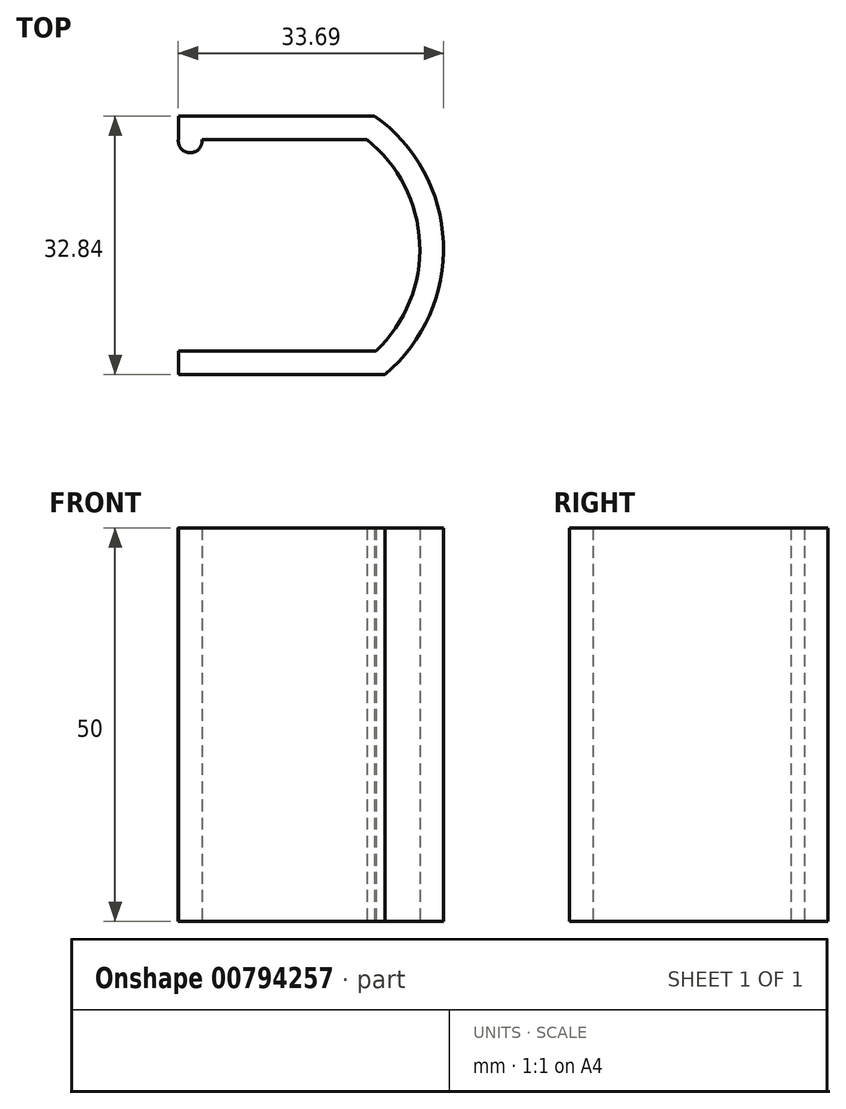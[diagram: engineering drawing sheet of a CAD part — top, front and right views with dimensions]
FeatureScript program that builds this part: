
annotation { "Feature Type Name" : "Feature", "Feature Type Description" : "" }
export const myFeature = defineFeature(function(context is Context, id is Id, definition is map)
    precondition{}
    {
        {
            var Q0;
            Q0=qCreatedBy(makeId("Top.planeOp"),FACE);
            var sketch = newSketch(context, id + "F0", { "sketchPlane" : qUnion([Q0])});
            skLineSegment(sketch, "E0", {"start": v(0, 0) * mm, "end": v(15.68, 0) * mm, "construction": true});
            skPoint(sketch, "E1", {"position": v(0, -13.42) * mm});
            skPoint(sketch, "E2", {"position": v(0, 13.42) * mm});
            skLineSegment(sketch, "E3", {"start": v(0, 13.42) * mm, "end": v(0, -13.42) * mm, "construction": true});
            skLineSegment(sketch, "E4", {"start": v(8.94, 13.42) * mm, "end": v(0, 13.42) * mm});
            skLineSegment(sketch, "E5", {"start": v(10.12, -13.42) * mm, "end": v(0, -13.42) * mm});
            skArc(sketch, "E6", {"start": v(10.13, -13.42) * mm, "mid": v(15.67, 0.27) * mm, "end": v(8.94, 13.42) * mm});
            skLineSegment(sketch, "E7.0", {"start": v(9.94, 16.42) * mm, "end": v(0, 16.42) * mm});
            skArc(sketch, "E7.1", {"start": v(11.27, -16.42) * mm, "mid": v(18.67, 0.33) * mm, "end": v(9.94, 16.42) * mm});
            skLineSegment(sketch, "E7.2", {"start": v(11.27, -16.42) * mm, "end": v(0, -16.42) * mm});
            skLineSegment(sketch, "E8", {"start": v(0, 16.42) * mm, "end": v(0, 13.42) * mm});
            skLineSegment(sketch, "E9", {"start": v(0, -13.42) * mm, "end": v(0, -16.42) * mm});
            skSolve(sketch);
        }
        {
            var Q0;
            Q0 = qSketchRegion(id + "F0", true);
            extrude(context, id + "F1", {"entities" : qUnion([Q0]), "depth" : 50 * mm, "offsetDistance" : 25 * mm});
        }
        {
            var Q0;
            Q0=makeQuery(id+"F1.opExtrude","SWEPT_FACE",FACE,{"disambiguationData":[OSD([sQuery(id+"F0.wireOp",EDGE,"E8")])]});
            var sketch = newSketch(context, id + "F2", { "sketchPlane" : qUnion([Q0])});
            skLineSegment(sketch, "E10.bottom", {"start": v(-16.42, 50) * mm, "end": v(-13.42, 50) * mm});
            skLineSegment(sketch, "E10.top", {"start": v(-16.42, 0) * mm, "end": v(-13.42, 0) * mm});
            skLineSegment(sketch, "E10.left", {"start": v(-16.42, 50) * mm, "end": v(-16.42, 0) * mm});
            skLineSegment(sketch, "E10.right", {"start": v(-13.42, 50) * mm, "end": v(-13.42, 0) * mm});
            skSolve(sketch);
        }
        {
            var Q0;
            Q0=makeQuery(id+"F2.imprint","IMPRINT",FACE,{"disambiguationData":[TD([[makeQuery(id+"F2.imprint","IMPRINT",EDGE,{"derivedFrom":sQuery(id+"F2.wireOp",EDGE,"E10.bottom")}),-1.0]])]});
            extrude(context, id + "F3", {"entities" : qUnion([Q0]), "operationType" : NewBodyOperationType.ADD, "depth" : 15 * mm, "offsetDistance" : 25 * mm});
        }
        {
            var Q0;
            Q0=makeQuery(id+"F1.opExtrude","SWEPT_FACE",FACE,{"disambiguationData":[OSD([sQuery(id+"F0.wireOp",EDGE,"E9")])]});
            var sketch = newSketch(context, id + "F4", { "sketchPlane" : qUnion([Q0])});
            skLineSegment(sketch, "E11.bottom", {"start": v(13.42, 50) * mm, "end": v(16.42, 50) * mm});
            skLineSegment(sketch, "E11.top", {"start": v(13.42, 0) * mm, "end": v(16.42, 0) * mm});
            skLineSegment(sketch, "E11.left", {"start": v(13.42, 50) * mm, "end": v(13.42, 0) * mm});
            skLineSegment(sketch, "E11.right", {"start": v(16.42, 50) * mm, "end": v(16.42, 0) * mm});
            skSolve(sketch);
        }
        {
            var Q0;
            Q0=makeQuery(id+"F4.imprint","IMPRINT",FACE,{"disambiguationData":[TD([[makeQuery(id+"F4.imprint","IMPRINT",EDGE,{"derivedFrom":sQuery(id+"F4.wireOp",EDGE,"E11.bottom")}),-1.0]])]});
            extrude(context, id + "F5", {"entities" : qUnion([Q0]), "operationType" : NewBodyOperationType.ADD, "depth" : 15 * mm, "offsetDistance" : 25 * mm});
        }
        {
            var Q0;
            Q0=makeQuery(id+"F1.opExtrude","SWEPT_EDGE",EDGE,{"disambiguationData":[OSD([sQuery(id+"F0.wireOp",EDGE,"E7.0"),sQuery(id+"F0.wireOp",EDGE,"E7.1")])]});
            cPlane(context, id + "F6", {"entities" : qUnion([Q0]), "cplaneType" : CPlaneType.LINE_ANGLE, "offset" : 25 * mm, "angle" : 67.06 * degree, "oppositeDirection" : true, "width" : 150 * mm, "height" : 150 * mm});
        }
        {
            var Q0;
            Q0=qCreatedBy(id+"F6.planeOp",FACE);
            var sketch = newSketch(context, id + "F7", { "sketchPlane" : qUnion([Q0])});
            skPoint(sketch, "E12", {"position": v(2.75, 13.58) * mm});
            skLineSegment(sketch, "E13.bottom", {"start": v(6.46, 11.07) * mm, "end": v(1.53, 9.28) * mm});
            skLineSegment(sketch, "E13.top", {"start": v(3.98, 17.89) * mm, "end": v(-0.95, 16.1) * mm});
            skLineSegment(sketch, "E13.left", {"start": v(7.65, 13.64) * mm, "end": v(6.54, 16.7) * mm});
            skLineSegment(sketch, "E13.right", {"start": v(-1.04, 10.47) * mm, "end": v(-2.15, 13.53) * mm});
            skPoint(sketch, "E14.visualSharp", {"position": v(-2.83, 15.4) * mm});
            skArc(sketch, "E14.filletArc", {"start": v(-0.95, 16.1) * mm, "mid": v(-2.08, 15.06) * mm, "end": v(-2.15, 13.53) * mm});
            skPoint(sketch, "E15.visualSharp", {"position": v(5.86, 18.57) * mm});
            skArc(sketch, "E15.filletArc", {"start": v(6.54, 16.7) * mm, "mid": v(5.5, 17.82) * mm, "end": v(3.98, 17.89) * mm});
            skPoint(sketch, "E16.visualSharp", {"position": v(8.34, 11.76) * mm});
            skArc(sketch, "E16.filletArc", {"start": v(6.46, 11.07) * mm, "mid": v(7.59, 12.1) * mm, "end": v(7.65, 13.64) * mm});
            skPoint(sketch, "E17.visualSharp", {"position": v(-0.35, 8.6) * mm});
            skArc(sketch, "E17.filletArc", {"start": v(-1.04, 10.47) * mm, "mid": v(0, 9.34) * mm, "end": v(1.53, 9.28) * mm});
            skLineSegment(sketch, "E18", {"start": v(-2.58, 14.34) * mm, "end": v(7.1, 15.16) * mm, "construction": true});
            skPoint(sketch, "E18.startSnap0", {"position": v(-1.6, 12) * mm});
            skSolve(sketch);
        }
        {
            var Q0;
            Q0=qCreatedBy(makeId("Top.planeOp"),FACE);
            var sketch = newSketch(context, id + "F8", { "sketchPlane" : qUnion([Q0])});
            skLineSegment(sketch, "E19", {"start": v(-15, 13.42) * mm, "end": v(-12, 13.42) * mm});
            skArc(sketch, "E20", {"start": v(-15, 13.42) * mm, "mid": v(-13.5, 11.74) * mm, "end": v(-12, 13.42) * mm});
            skSolve(sketch);
        }
        {
            var Q0;
            Q0=makeQuery(id+"F8.imprint","IMPRINT",FACE,{"disambiguationData":[TD([[makeQuery(id+"F8.imprint","IMPRINT",EDGE,{"derivedFrom":sQuery(id+"F8.wireOp",EDGE,"E19")}),-1.0]])]});
            extrude(context, id + "F9", {"entities" : qUnion([Q0]), "operationType" : NewBodyOperationType.ADD, "depth" : 50 * mm, "offsetDistance" : 25 * mm});
        }
    });
